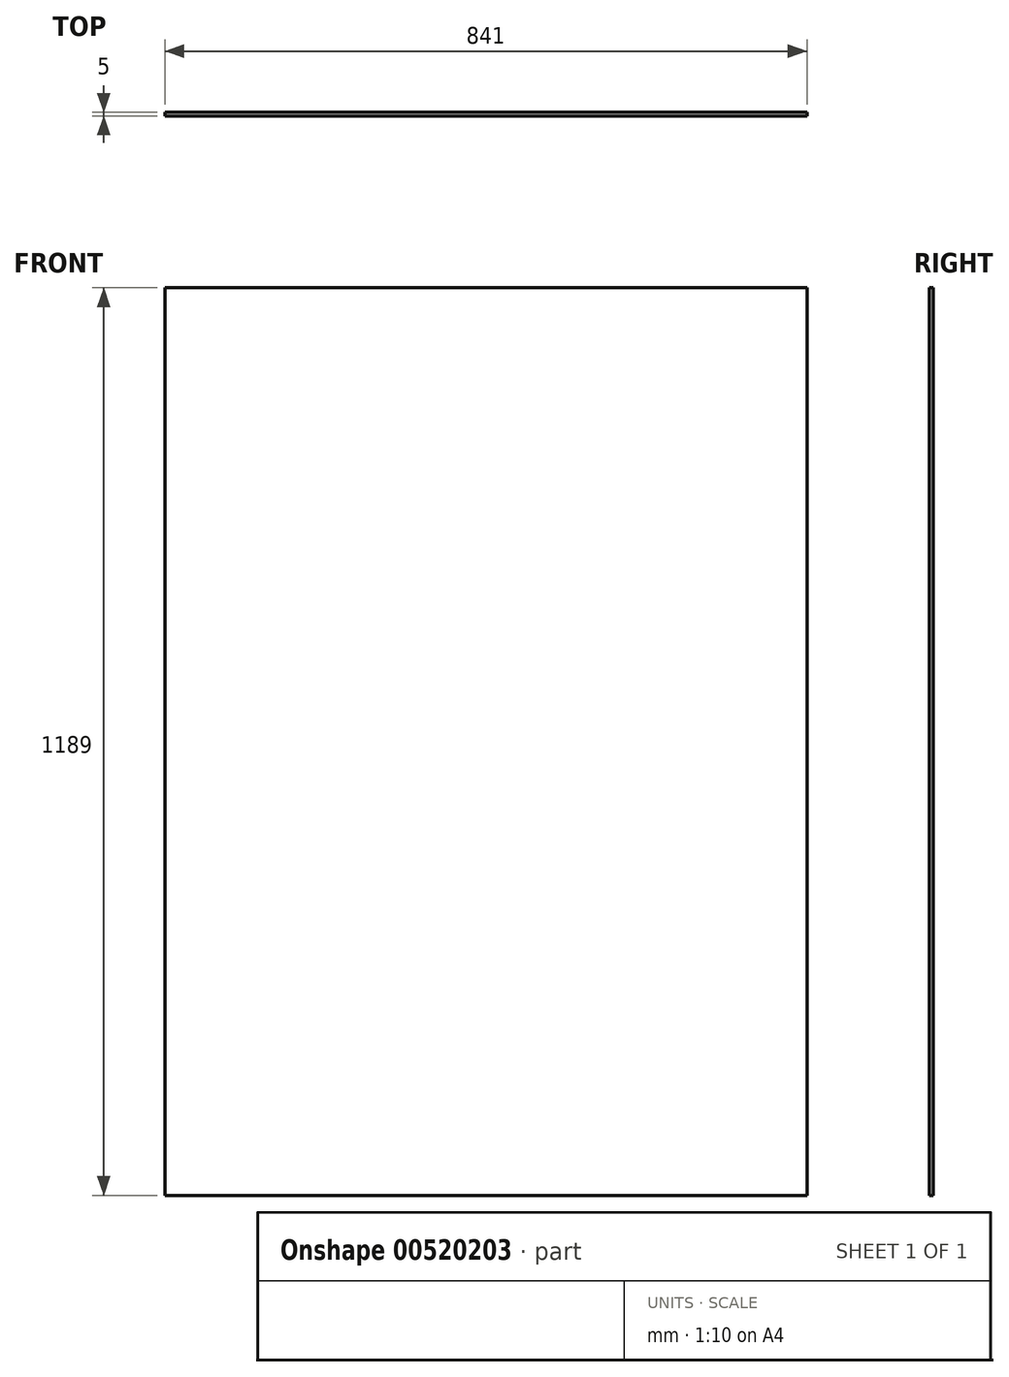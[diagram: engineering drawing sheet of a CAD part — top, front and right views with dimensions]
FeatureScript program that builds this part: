
annotation { "Feature Type Name" : "Feature", "Feature Type Description" : "" }
export const myFeature = defineFeature(function(context is Context, id is Id, definition is map)
    precondition{}
    {
        {
            var Q0;
            Q0=qCreatedBy(makeId("Front.planeOp"),FACE);
            var sketch = newSketch(context, id + "F0", { "sketchPlane" : qUnion([Q0])});
            skLineSegment(sketch, "E0.bottom", {"start": v(-420.5, 594.5) * mm, "end": v(420.5, 594.5) * mm});
            skLineSegment(sketch, "E0.top", {"start": v(-420.5, -594.5) * mm, "end": v(420.5, -594.5) * mm});
            skLineSegment(sketch, "E0.left", {"start": v(-420.5, 594.5) * mm, "end": v(-420.5, -594.5) * mm});
            skLineSegment(sketch, "E0.right", {"start": v(420.5, 594.5) * mm, "end": v(420.5, -594.5) * mm});
            skPoint(sketch, "E0.middle", {"position": v(0, 0) * mm});
            skSolve(sketch);
        }
        {
            var Q0;
            Q0 = qSketchRegion(id + "F0", true);
            extrude(context, id + "F1", {"entities" : qUnion([Q0]), "depth" : 5 * mm, "offsetDistance" : 25 * mm});
        }
    });
